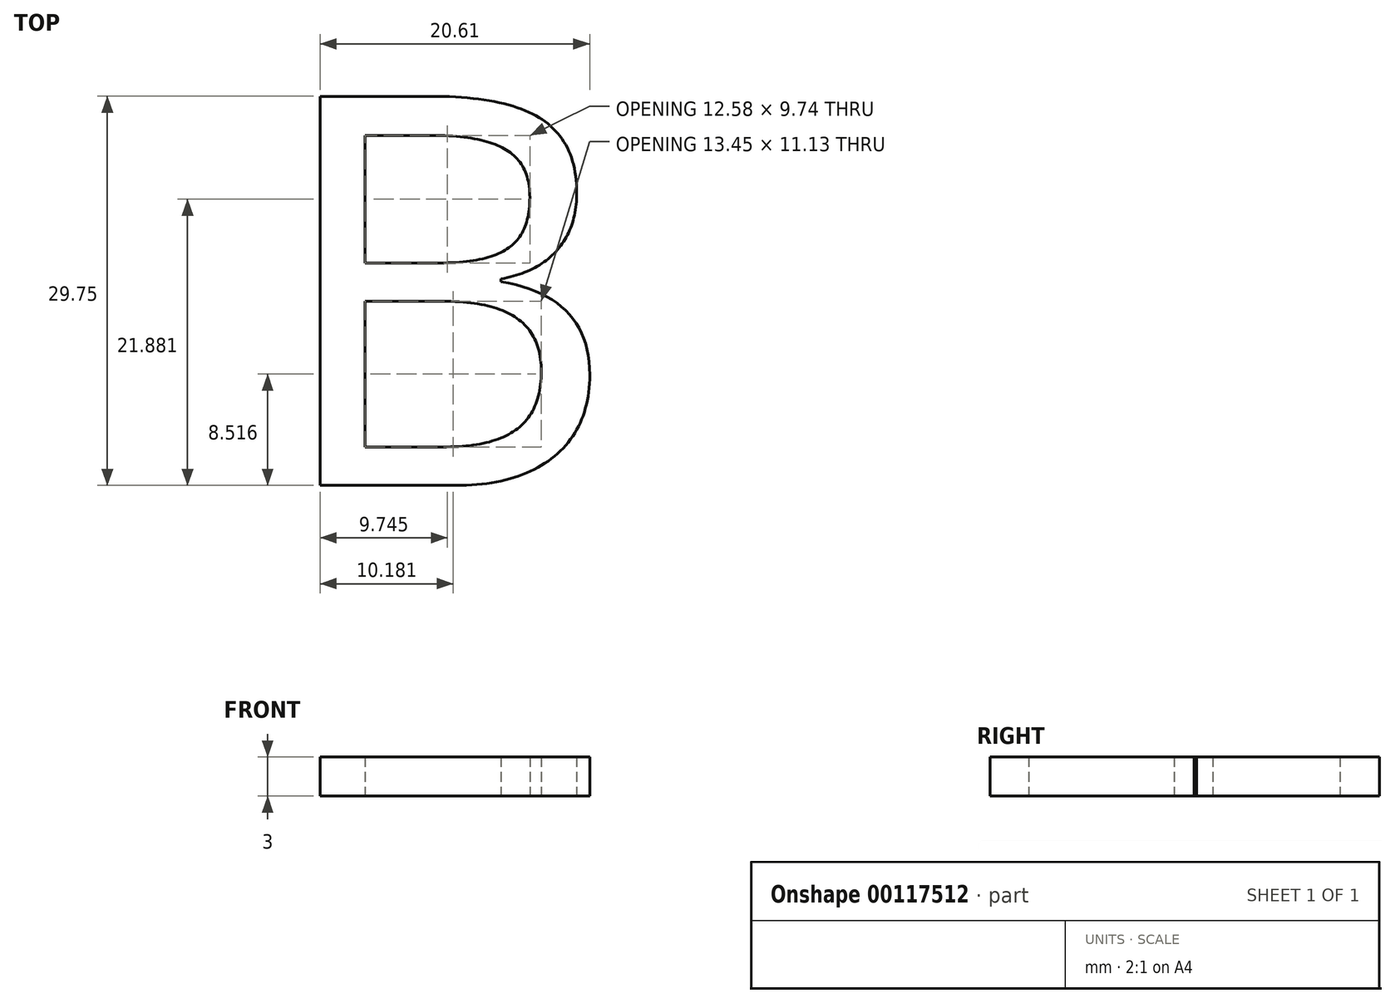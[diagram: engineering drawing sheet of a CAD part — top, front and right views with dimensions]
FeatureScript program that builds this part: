
annotation { "Feature Type Name" : "Feature", "Feature Type Description" : "" }
export const myFeature = defineFeature(function(context is Context, id is Id, definition is map)
    precondition{}
    {
        {
            var Q0;
            Q0=qCreatedBy(makeId("Top.planeOp"),FACE);
            var sketch = newSketch(context, id + "F0", { "sketchPlane" : qUnion([Q0])});
            skText(sketch, "E0", { "text": "B", "fontName": "OpenSans-Regular.ttf"});
            const initialGuessF0  = {"E0": [0, 0, 1, 0, 0.03]};
            skSetInitialGuess(sketch, initialGuessF0);
            skSolve(sketch);
        }
        {
            var Q0;
            Q0 = qSketchRegion(id + "F0", true);
            extrude(context, id + "F1", {"entities" : qUnion([Q0]), "depth" : 3 * mm});
        }
    });
